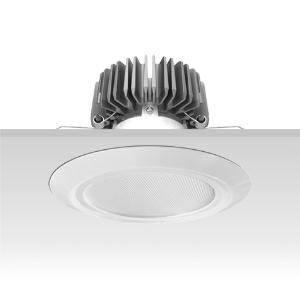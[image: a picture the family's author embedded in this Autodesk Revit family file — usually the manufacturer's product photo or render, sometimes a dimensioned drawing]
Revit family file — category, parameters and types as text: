
# Revit family: 3f_filippi_-_3f_reno_bianco_ampio_3f_filippi_-_30629_a01037_-_3f_reno_200_wh_3000-840_wide___vs_wh_c2fa
name_source: partatom
category: Lighting Fixtures
units: mm (PartAtom-declared; Revit-internal decimal feet)

## family parameters
Cut with Voids When Loaded = No
Host = Face
Light Source = No
Part Type = Normal
Room Calculation Point = No
Round Connector Dimension = Use Diameter
Shared = No

## types (1)
- 3F Filippi - 3F Reno Bianco Ampio (1 x LED, 2312 lm, 28 W, 4000 K)
    Apparent Load = 28 VA
    Approval mark = CE
    CIE Flux Codes = 75 94 99 100 100
    Color Rendering = 80
    Color Temperature = 4000 K
    Control Gear = Electronic ballast
    Default Elevation = 1800 mm
    Description = ILLUMINOTECHNICAL
Luminous efficiency 100% (DLOR 100%, ULOR 0%).
Initial luminous flux of the luminaire 2312 lm.
Direct symmetric wide distribution.
Installation Interdistance Transv.D = 1.16 x hu - Long.D = 1.14 x hu.
Tabular UGR (CIE 117 - 4H-8H; S=0.25H; 70/50/20): RUG 21.5 - 21.4.
Beam angle: 74° - 74°.
Luminous efficacy 83 lm/W.
Lifetime (L90/B10): 30000 h. (tq+25°C)
Lifetime (L85/B10): 50000 h. (tq+25°C)
Lifetime (L70/B10): 80000 h. (tq+25°C)
Sudden decreased luminous flux after 50000 hours: 0% (C0).
Photobiological safety in compliance with IEC/TR 62778: RG0 risk exempt, (IEC 62471).
In compliance with IEC/EN 62722-2-1 - IEC/EN 62717 standards.

SOURCE
Compact LED module 3000/840.
Energy efficiency class (UE 2019/2020 - UE 2019/2015): D.
CIE 13.3 Colour rendering index: CRI >80 (R9 <50%).
IES TM-30 Fidelity Index: Rf = 84 Rg = 95.
CCT nominal colour temperature 4000 K.
Colour initial tolerance (MacAdam): SDCM 3.
Zhaga Book 3 compliant.

MECHANICAL
Passive heat dissipator in die-casting aluminium, oversized, for optimum thermal management of the LED module.
Parabolic element with graduated/concentric rings in white polycarbonate.
Transparent external lens with glossy and satin differentiated surfaces, with a cooling and anti-insect system in methacrylate (PMMA).
Fastening spring clips in stainless steel.
Dimensions: diameter 226 mm, height 146 mm. Weight 1.785 kg.
IP44 protection degree for exposed part, IP20 for recessed part.
Mechanical strength to impacts IK06 (1 joule).
Glow-wire test resistance 650°C.

ELECTRICAL
Wiring on a separate unit.
Halogen Free electronic wiring 230V-50/60Hz, power factor 0.95, THD <25%, constant output current, SELV, class II, 1 driver.
Power of the luminaire 28 W.
ENEC - CE.
SAFE FLICKER: PstLM=<1 and SVM=<0.4 (IEC TR 61547-1 and IEC TR 63158), to ensure a more comfortable and safe light.
Luminaire compliant with EN 60598-2-22 for power supply from a centralised emergency system CPSS (Central Power Supply System), not incorporated in the luminaire - high risk areas excluded. The default power and flux are 100% in AC and 100% in DC.
Ambient temperature from 0°C to +25°C.
Temperature class T6 max 85°C.
Relative humidity UR: <85%.

INSTALLATION
Pull-up recessed fitting.
False ceiling carving: 200 mm.
All accessories dedicated to this product are available on the Catalog and on our website www.3F-Filippi.com.

ACCESSORIES
A01037 - Anti-glare microprismatic VS moulded glass, tempered, not flammable, locked and in line with the trim, in white polycarbonate.

APPLICATIONS
Environments: architectural, commercial, exhibition areas, transit areas, corridors, shops, display windows, service areas.
In false ceilings with narrow voids.

WARNING
Luminaire designed for disposal/recycling at end-of-life.
Replaceable (LED only) light source by a professional. Replaceable control gear by a professional.
    Height = 0 mm  [stored 0 ft]
    Lamp = 1 x LED
    Lamp Light Flux = 2312 lm
    Lamp Power = 28 W
    Lamp count = 1
    Length = 226 mm
    Lifetime = 50000 h
    Luminous efficacy = 83 lm/W
    Manufacturer = 3F Filippi
    ModVariant = No
    Model = 3F Filippi - 30629+A01037 - 3F Reno 200 WH 3000-840 WIDE + VS WH
    Mounting Place = Ceiling
    Mounting Type = Recessed
    Number of Poles = 1
    OnlyDefault = Yes
    Power Factor = 1
    Product Name = 3F Filippi - 3F Reno Bianco Ampio
    Product group = recessed luminaire
    ProductGroupID = 4
    Protection Class = Protection class II
    Protection Degree = IP 20
    RLX_Detail_Level = 1
    RLX_Emergency_Light_Flux = 0 lm
    RLX_Emergency_Type = 0
    RLX_Emergency_Type_DB = No
    RlxData = <blob elided: 94217 chars, md5=5ad24f47>
    Socket = socket
    Standby Power = 0 W
    System Light Flux = 2312 lm
    System Power = 28 W
    Type Comments = Product without accessories
    Type Image = 3ffilippi_3f_reno_200_wh_vs_smp.jpg
    URL = http://relux.com
    VarID = ---
    Voltage = 0 V
    Weight = 0.00 kg
    Width = 0 mm  [stored 0 ft]

note: [stored X ft] marks values corroborated as IEEE doubles in the binary element streams (Revit-internal decimal feet)

## geometry (parser evidence)
native form markers: Blend x4, Sweep x9
no freeform markers — native parametric forms only
